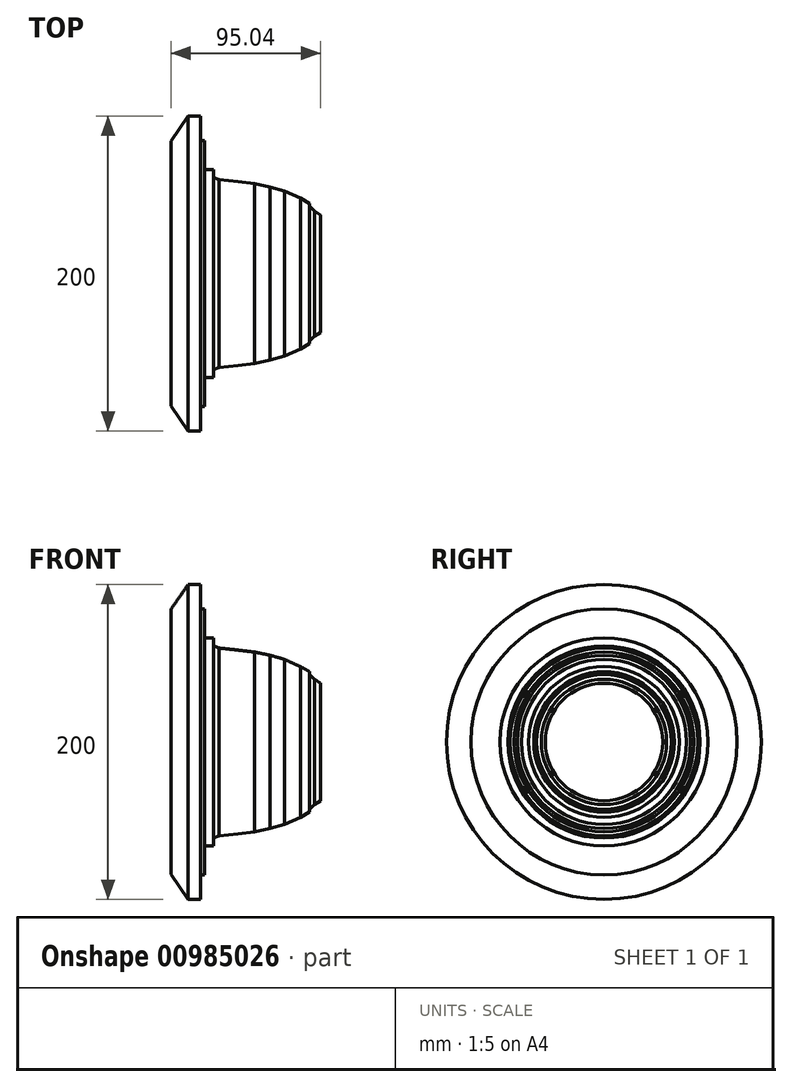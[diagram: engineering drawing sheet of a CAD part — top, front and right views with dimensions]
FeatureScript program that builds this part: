
annotation { "Feature Type Name" : "Feature", "Feature Type Description" : "" }
export const myFeature = defineFeature(function(context is Context, id is Id, definition is map)
    precondition{}
    {
        {
            var Q0;
            Q0=qCreatedBy(makeId("Front.planeOp"),FACE);
            var sketch = newSketch(context, id + "F0", { "sketchPlane" : qUnion([Q0])});
            skLineSegment(sketch, "E0", {"start": v(-8.4, 60.86) * mm, "end": v(-8.4, -139.14) * mm});
            skLineSegment(sketch, "E1", {"start": v(-8.4, 45.36) * mm, "end": v(-5.87, 45.36) * mm});
            skLineSegment(sketch, "E2", {"start": v(-5.87, 45.36) * mm, "end": v(-5.87, 26.86) * mm});
            skLineSegment(sketch, "E3", {"start": v(-5.87, 26.86) * mm, "end": v(0, 26.86) * mm});
            skLineSegment(sketch, "E4", {"start": v(0, 26.86) * mm, "end": v(0, 21.95) * mm});
            skLineSegment(sketch, "E5", {"start": v(0, 21.95) * mm, "end": v(3.4, 20.52) * mm});
            skLineSegment(sketch, "E6", {"start": v(3.4, 20.52) * mm, "end": v(15.62, 19.18) * mm});
            skLineSegment(sketch, "E7", {"start": v(15.62, 19.18) * mm, "end": v(26, 17.96) * mm});
            skLineSegment(sketch, "E8", {"start": v(26, 17.96) * mm, "end": v(35.98, 15.9) * mm});
            skLineSegment(sketch, "E9", {"start": v(35.98, 15.9) * mm, "end": v(45.1, 13.29) * mm});
            skLineSegment(sketch, "E10", {"start": v(45.1, 13.29) * mm, "end": v(55.18, 8.73) * mm});
            skLineSegment(sketch, "E11", {"start": v(55.18, 8.73) * mm, "end": v(61.01, 5.45) * mm});
            skLineSegment(sketch, "E12", {"start": v(61.01, 5.45) * mm, "end": v(61.01, 3.62) * mm});
            skLineSegment(sketch, "E13", {"start": v(61.01, 3.62) * mm, "end": v(64.05, 0.65) * mm});
            skLineSegment(sketch, "E14", {"start": v(64.05, 0.65) * mm, "end": v(67.94, -1.85) * mm});
            skLineSegment(sketch, "E15", {"start": v(67.94, -1.85) * mm, "end": v(67.94, -48.78) * mm});
            skLineSegment(sketch, "E16", {"start": v(-8.4, -39.14) * mm, "end": v(67.94, -39.14) * mm});
            skLineSegment(sketch, "E17", {"start": v(-8.4, 60.86) * mm, "end": v(-16.11, 60.86) * mm});
            skLineSegment(sketch, "E18", {"start": v(-16.11, 60.86) * mm, "end": v(-27.1, 45.08) * mm});
            skLineSegment(sketch, "E19", {"start": v(-27.1, 45.08) * mm, "end": v(-27.1, -39.14) * mm});
            skLineSegment(sketch, "E20", {"start": v(-27.1, -39.14) * mm, "end": v(-8.4, -39.14) * mm});
            skSolve(sketch);
        }
        {
            var Q0;
            {var subQ0=sQuery(id+"F0.wireOp",EDGE,"E17");Q0=makeQuery(id+"F0.imprint","IMPRINT",FACE,{"disambiguationData":[TD([[makeQuery(id+"F0.imprint","IMPRINT",EDGE,{"derivedFrom":subQ0}),1.0]])]});}
            var Q1;
            {var subQ0=sQuery(id+"F0.wireOp",EDGE,"E1");Q1=makeQuery(id+"F0.imprint","IMPRINT",FACE,{"disambiguationData":[TD([[makeQuery(id+"F0.imprint","IMPRINT",EDGE,{"derivedFrom":subQ0}),-1.0]])]});}
            var Q2;
            Q2=sQuery(id+"F0.wireOp",EDGE,"E16");
            revolve(context, id + "F1", {"surfaceOperationType" : NewSurfaceOperationType.NEW, "entities" : qUnion([Q0, Q1]), "axis" : qUnion([Q2]), "revolveType" : RevolveType.FULL});
        }
    });
